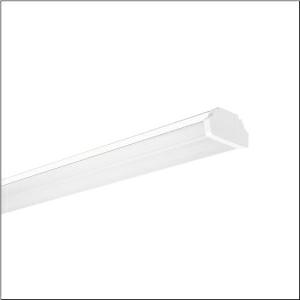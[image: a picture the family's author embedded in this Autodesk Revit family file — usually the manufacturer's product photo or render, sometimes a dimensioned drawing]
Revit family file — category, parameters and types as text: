
# Revit family: dus_31_gen_2_53bd812cv685c2_b411
name_source: partatom
category: Lighting Fixtures
units: mm (PartAtom-declared; Revit-internal decimal feet)

## family parameters
Cut with Voids When Loaded = No
Host = Face
Light Source = No
Part Type = Normal
Room Calculation Point = No
Round Connector Dimension = Use Diameter
Shared = No

## types (1)
- --- (1 x LED, 8970 lm, 49.9 W, 6500K)
    Apparent Load = 50 VA
    CIE Flux Codes = 47 80 95 93 100
    Color Rendering = 80
    Color Temperature = 6500K
    Default Elevation = 1800 mm
    Description = DUS 31 Gen.2, luminaire insert, of sheet steel, coil coated, white, length: 1.535mm, width: 81mm, height: 90mm, 5x system unit, system units: 307mm, LED rated luminous flux: 8.970lm, light colour: 865, SDCM (Standard Deviation of Colour Matching)MacAdam ≤ 3 SDCM (initial), control gear: ON/OFF Multilumen, CLOi, with plug, 3-pole, with phase selection, mains connection: 220..240V, AC, 50/60Hz, start of lifetime: 50W, end of service life: 61W, through-wiring accessed according to module size, primary optical cover: cover, of PMMA, light emission: direct distribution, primary light characteristic: symmetric, protection rating (complete): IP20, protection rating (LED compartment): IP50, insulation class (complete): insulation class I (protective earthing), certification: CE, ENEC, VDE, UKCA, impact resistance: IK03, permissible ambient temperature for indoor applications: -35..+40°C, corresponds to IFS (International Featured Standards) requirements for safety and quality in the food industry, reducing of maximum allowable ambient temperature of 5°C with ceiling mounting, packaging unit: 1 piece
    Height = 95 mm
    Lamp = 1 x LED
    Lamp Light Flux = 8970 lm
    Lamp Power = 49.9 W
    Lamp count = 1
    Length = 1535 mm
    Luminous efficacy = 180 lm/W
    Manufacturer = Siteco
    ModVariant = No
    Model = 53BD812CV685C2
    Mounting Place = Ceiling
    Mounting Type = Pendant
    Number of Poles = 1
    OnlyDefault = Yes
    Power Factor = 1
    Product Name = DUS 31 Gen.2
    Product group = luminaire insert | ceiling pendant
    ProductGroupID = 901
    Protection Class = Protection class I
    Protection Degree = IP 20
    RLX_Detail_Level = 1
    RLX_Emergency_Light_Flux = 0 lm
    RLX_Emergency_Type = 0
    RLX_Emergency_Type_DB = No
    RlxData = <blob elided: 29833 chars, md5=47561a56>
    Socket = socket
    Standby Power = 0 W
    System Light Flux = 8970 lm
    System Power = 50 W
    Type Comments = factory setting: luminous flux: 100 % | (A | C | E) | 116 mA
    Type Image = l_1319596.jpg
    URL = http://relux.com
    VarID = @adj_051237
    Voltage = 0 V
    Weight = 0.00 kg
    Width = 81 mm

## geometry (parser evidence)
native form markers: Blend x4, Sweep x13
no freeform markers — native parametric forms only
